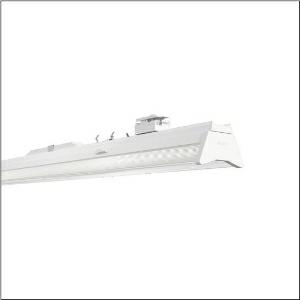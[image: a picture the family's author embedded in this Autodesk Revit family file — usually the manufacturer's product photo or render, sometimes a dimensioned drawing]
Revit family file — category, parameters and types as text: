
# Revit family: licross_r__21_performance_mo_52tm16dn4a5g_341e
name_source: partatom
category: Lighting Fixtures
units: mm (PartAtom-declared; Revit-internal decimal feet)

## family parameters
Cut with Voids When Loaded = No
Host = Face
Light Source = No
Part Type = Normal
Room Calculation Point = No
Round Connector Dimension = Use Diameter
Shared = No

## types (1)
- --- (1 x LED, 10840 lm, 62 W, 4000K)
    Apparent Load = 62 VA
    CIE Flux Codes = 66 88 96 79 100
    Color Rendering = 80
    Color Temperature = 4000K
    Default Elevation = 1800 mm
    Description = Licross® 21 Performance MO, luminaire insert, of sheet steel, galvanised, coil coated, white, length: 1.500mm, width: 120mm, height: 123mm, LED rated luminous flux: 10.840lm, light colour: 840, control gear: DALI 2, control gear: ECG DALI, with plug, 5-pole, with phase selection, mains connection: 220..240V, AC, 50/60Hz, halogen-free wiring, primary light control with lens, of plastic, primary optical cover: cover, of PMMA, light emission: direct/indirect distribution, primary light characteristic: symmetric, protection rating (complete): IP40, insulation class (complete): insulation class I (protective earthing), certification: CE, ENEC, UKCA, protection symbol: D if used in an environment without relevant dust loads with corresponding accessories, impact resistance: IK06, permissible ambient temperature for indoor applications: -25..+35°C, corresponds to IFS (International Featured Standards) requirements for safety and quality in the food industry, reducing of maximum allowable ambient temperature of 5°C with ceiling mounting, LABS conformity tested according to VDMA 24364:2018-05, packaging unit: 1 piece
    Height = 114 mm
    Lamp = 1 x LED
    Lamp Light Flux = 10840 lm
    Lamp Power = 62 W
    Lamp count = 1
    Length = 1500 mm
    Luminous efficacy = 175 lm/W
    Manufacturer = Siteco
    ModVariant = No
    Model = 52TM16DN4A5G
    Mounting Place = Ceiling
    Mounting Type = Pendant
    Number of Poles = 1
    OnlyDefault = Yes
    Power Factor = 1
    Product Name = Licross® 21 Performance MO
    Product group = luminaire insert
    ProductGroupID = 902
    Protection Class = Protection class I
    Protection Degree = IP 40
    RLX_Detail_Level = 1
    RlxData = <blob elided: 34161 chars, md5=ac3dce09>
    Socket = socket
    Standby Power = 0 W
    System Light Flux = 10840 lm
    System Power = 62 W
    Type Comments = factory setting: luminous flux: 100 % | dim-lin: 254 | 418 mA
    Type Image = l_1256138.jpg
    URL = http://relux.com
    VarID = @adj_039511
    Voltage = 0 V
    Weight = 0.00 kg
    Width = 120 mm

## geometry (parser evidence)
native form markers: Blend x4, Sweep x12
no freeform markers — native parametric forms only
